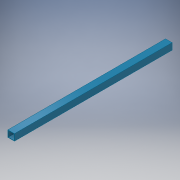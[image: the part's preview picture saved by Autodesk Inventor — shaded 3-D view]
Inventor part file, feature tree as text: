
AUTODESK INVENTOR PART (.ipt)
format: ipt  version: 2017 SP1 (Build 210196100, 196)  size: 99,328 bytes
history: native  units: in
note: dims shown in document units (in); Inventor stores cm internally (conversion verified against a paired STEP export)
features: extrude x1, sketch x1
ambient origin geometry x8: Origin, YZ Plane, XZ Plane, XY Plane, X Axis, Y Axis, Z Axis, Center Point
bodies: Solid1 (feature_tree)
feature tree (2):
  extrude  "Extrusion1"  Depth=1.0in
  sketch  "Sketch1"  dims[d0=1.0in d1=1.0in d2=0.0625in d3=24.0in d4=0.0in]
